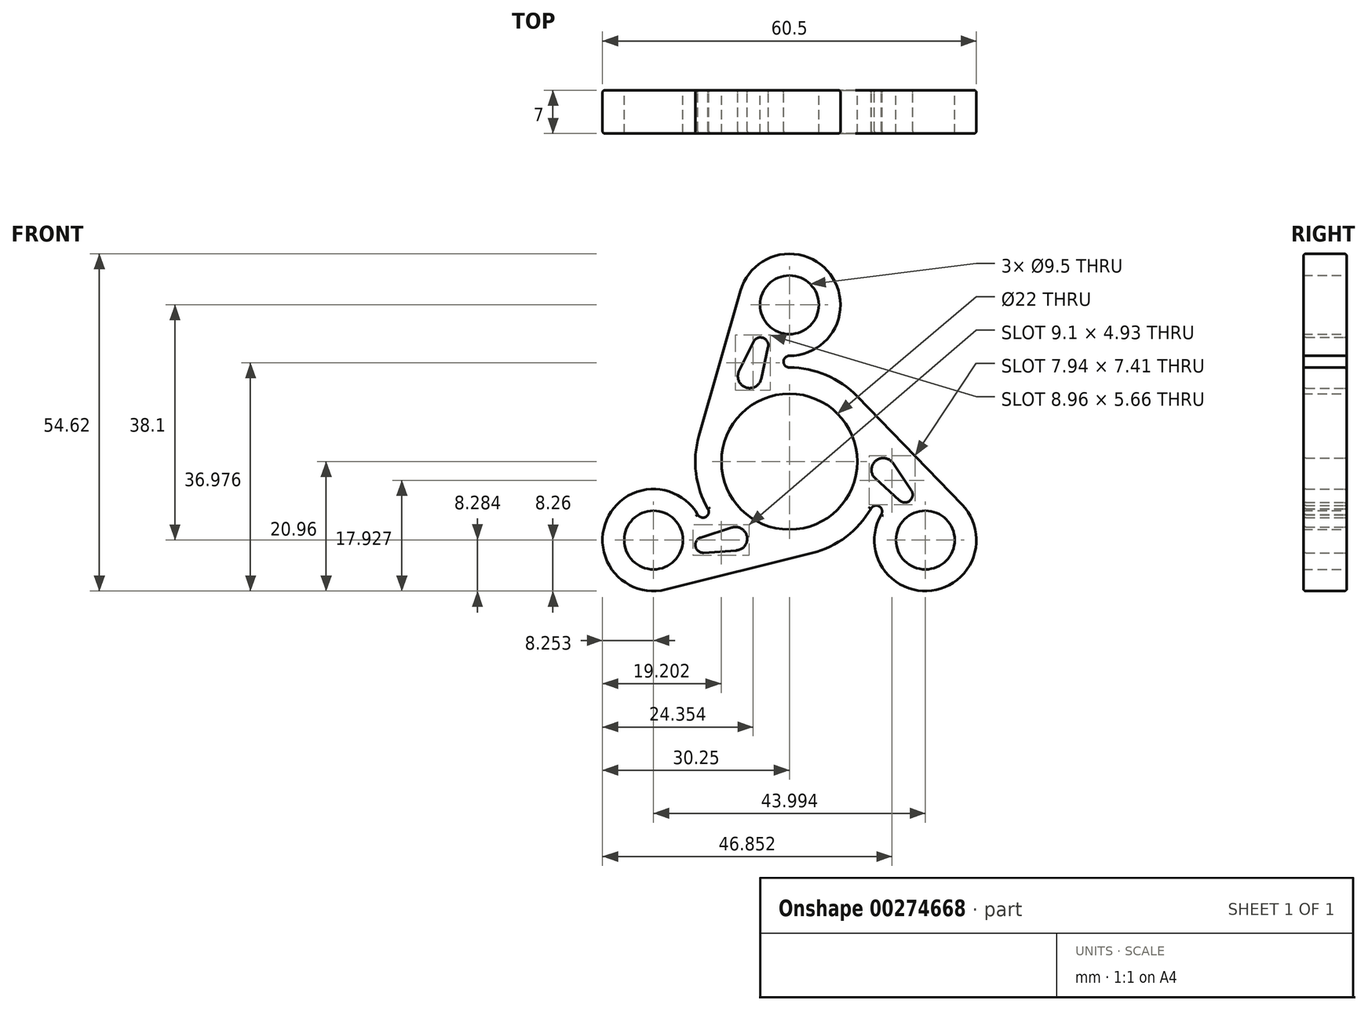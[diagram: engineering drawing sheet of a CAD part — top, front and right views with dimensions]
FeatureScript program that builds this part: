
annotation { "Feature Type Name" : "Feature", "Feature Type Description" : "" }
export const myFeature = defineFeature(function(context is Context, id is Id, definition is map)
    precondition{}
    {
        {
            var Q0;
            Q0=qCreatedBy(makeId("Front.planeOp"),FACE);
            var sketch = newSketch(context, id + "F0", { "sketchPlane" : qUnion([Q0])});
            skCircle(sketch, "E0", {"center": v(0, 0) * mm, "radius": 11 * mm});
            skArc(sketch, "E1", {"start": v(-14.65, 4.2) * mm, "mid": v(-15.12, -1.88) * mm, "end": v(-13.18, -7.66) * mm});
            skLineSegment(sketch, "E2", {"start": v(0, 0) * mm, "end": v(-45.3, -26.16) * mm, "construction": true});
            skLineSegment(sketch, "E3", {"start": v(0, 0) * mm, "end": v(47.1, -27.19) * mm, "construction": true});
            skCircle(sketch, "E4", {"center": v(0, 0) * mm, "radius": 25.4 * mm, "construction": true});
            skCircle(sketch, "E5", {"center": v(0, 25.4) * mm, "radius": 4.75 * mm});
            skCircle(sketch, "E6", {"center": v(-22, -12.7) * mm, "radius": 4.75 * mm});
            skCircle(sketch, "E7", {"center": v(22, -12.7) * mm, "radius": 4.75 * mm});
            skArc(sketch, "E8", {"start": v(0, 17.14) * mm, "mid": v(6.6, 30.37) * mm, "end": v(-7.94, 27.67) * mm});
            skArc(sketch, "E9", {"start": v(-14.83, -8.6) * mm, "mid": v(-29.59, -9.46) * mm, "end": v(-20, -20.7) * mm});
            skArc(sketch, "E10", {"start": v(14.85, -8.57) * mm, "mid": v(23, -20.9) * mm, "end": v(27.93, -6.96) * mm});
            skLineSegment(sketch, "E11", {"start": v(-7.94, 27.67) * mm, "end": v(-14.65, 4.2) * mm});
            skLineSegment(sketch, "E12", {"start": v(-20, -20.7) * mm, "end": v(3.7, -14.78) * mm});
            skLineSegment(sketch, "E13", {"start": v(27.93, -6.96) * mm, "end": v(10.96, 10.6) * mm});
            skArc(sketch, "E14.trimOffspring", {"start": v(10.96, 10.6) * mm, "mid": v(5.95, 14.03) * mm, "end": v(0, 15.24) * mm});
            skArc(sketch, "E15.trimOffspring", {"start": v(3.7, -14.78) * mm, "mid": v(9.18, -12.17) * mm, "end": v(13.2, -7.62) * mm});
            skArc(sketch, "E16", {"start": v(-8.15, 14.65) * mm, "mid": v(-7.06, 12.01) * mm, "end": v(-4.58, 13.4) * mm});
            skLineSegment(sketch, "E17", {"start": v(-6.44, 13.81) * mm, "end": v(0, 0) * mm, "construction": true});
            skArc(sketch, "E18", {"start": v(-3.46, 18.58) * mm, "mid": v(-4.28, 20.05) * mm, "end": v(-5.84, 19.4) * mm});
            skLineSegment(sketch, "E19", {"start": v(-3.46, 18.58) * mm, "end": v(-4.58, 13.4) * mm});
            skLineSegment(sketch, "E20", {"start": v(-5.84, 19.4) * mm, "end": v(-8.15, 14.65) * mm});
            skLineSegment(sketch, "E21.1.0", {"start": v(-13.88, -14.76) * mm, "end": v(-8.6, -14.38) * mm});
            skArc(sketch, "E21.1.1", {"start": v(-14.36, -12.28) * mm, "mid": v(-15.22, -13.73) * mm, "end": v(-13.88, -14.76) * mm});
            skLineSegment(sketch, "E21.1.2", {"start": v(-14.36, -12.28) * mm, "end": v(-9.32, -10.67) * mm});
            skArc(sketch, "E21.1.3", {"start": v(-8.6, -14.38) * mm, "mid": v(-6.87, -12.12) * mm, "end": v(-9.32, -10.67) * mm});
            skLineSegment(sketch, "E21.2.0", {"start": v(19.72, -4.64) * mm, "end": v(16.76, -0.26) * mm});
            skArc(sketch, "E21.2.1", {"start": v(17.82, -6.3) * mm, "mid": v(19.5, -6.31) * mm, "end": v(19.72, -4.64) * mm});
            skLineSegment(sketch, "E21.2.2", {"start": v(17.82, -6.3) * mm, "end": v(13.9, -2.74) * mm});
            skArc(sketch, "E21.2.3", {"start": v(16.76, -0.26) * mm, "mid": v(13.93, 0.11) * mm, "end": v(13.9, -2.74) * mm});
            skLineSegment(sketch, "E22", {"start": v(0, 0) * mm, "end": v(-4.7, 18.85) * mm, "construction": true});
            skArc(sketch, "E23", {"start": v(-14.85, -8.57) * mm, "mid": v(-13.54, -8.94) * mm, "end": v(-13.2, -7.62) * mm});
            skArc(sketch, "E24", {"start": v(0, 17.14) * mm, "mid": v(-0.95, 16.2) * mm, "end": v(0, 15.24) * mm});
            skArc(sketch, "E25", {"start": v(14.85, -8.57) * mm, "mid": v(14.52, -7.23) * mm, "end": v(13.2, -7.62) * mm});
            skSolve(sketch);
        }
        {
            var Q0;
            Q0 = qSketchRegion(id + "F0", true);
            extrude(context, id + "F1", {"entities" : qUnion([Q0]), "depth" : 7 * mm, "offsetDistance" : 25.4 * mm});
        }
        {
            var Q0;
            Q0=makeQuery(id+"F1.opExtrude","CAP_EDGE",EDGE,{"disambiguationData":[OSD([sQuery(id+"F0.wireOp",EDGE,"E1")])],"isStart":false});
            var Q1;
            Q1=makeQuery(id+"F1.opExtrude","CAP_EDGE",EDGE,{"disambiguationData":[OSD([sQuery(id+"F0.wireOp",EDGE,"E11")])],"isStart":false});
            var Q2;
            Q2=makeQuery(id+"F1.opExtrude","CAP_EDGE",EDGE,{"disambiguationData":[OSD([sQuery(id+"F0.wireOp",EDGE,"E16")])],"isStart":false});
            var Q3;
            Q3=makeQuery(id+"F1.opExtrude","CAP_EDGE",EDGE,{"disambiguationData":[OSD([sQuery(id+"F0.wireOp",EDGE,"E19")])],"isStart":false});
            var Q4;
            Q4=makeQuery(id+"F1.opExtrude","CAP_EDGE",EDGE,{"disambiguationData":[OSD([sQuery(id+"F0.wireOp",EDGE,"E20")])],"isStart":false});
            var Q5;
            Q5=makeQuery(id+"F1.opExtrude","CAP_EDGE",EDGE,{"disambiguationData":[OSD([sQuery(id+"F0.wireOp",EDGE,"E18")])],"isStart":false});
            var Q6;
            Q6=makeQuery(id+"F1.opExtrude","CAP_EDGE",EDGE,{"disambiguationData":[OSD([sQuery(id+"F0.wireOp",EDGE,"E8")])],"isStart":false});
            var Q7;
            Q7=makeQuery(id+"F1.opExtrude","CAP_EDGE",EDGE,{"disambiguationData":[OSD([sQuery(id+"F0.wireOp",EDGE,"E24")])],"isStart":false});
            var Q8;
            Q8=makeQuery(id+"F1.opExtrude","CAP_EDGE",EDGE,{"disambiguationData":[OSD([sQuery(id+"F0.wireOp",EDGE,"E14.trimOffspring")])],"isStart":false});
            var Q9;
            Q9=makeQuery(id+"F1.opExtrude","CAP_EDGE",EDGE,{"disambiguationData":[OSD([sQuery(id+"F0.wireOp",EDGE,"E13")])],"isStart":false});
            var Q10;
            Q10=makeQuery(id+"F1.opExtrude","CAP_EDGE",EDGE,{"disambiguationData":[OSD([sQuery(id+"F0.wireOp",EDGE,"E25")])],"isStart":false});
            var Q11;
            Q11=makeQuery(id+"F1.opExtrude","CAP_EDGE",EDGE,{"disambiguationData":[OSD([sQuery(id+"F0.wireOp",EDGE,"E15.trimOffspring")])],"isStart":false});
            var Q12;
            Q12=makeQuery(id+"F1.opExtrude","CAP_EDGE",EDGE,{"disambiguationData":[OSD([sQuery(id+"F0.wireOp",EDGE,"E21.2.3")])],"isStart":false});
            var Q13;
            Q13=makeQuery(id+"F1.opExtrude","CAP_EDGE",EDGE,{"disambiguationData":[OSD([sQuery(id+"F0.wireOp",EDGE,"E21.2.2")])],"isStart":false});
            var Q14;
            Q14=makeQuery(id+"F1.opExtrude","CAP_EDGE",EDGE,{"disambiguationData":[OSD([sQuery(id+"F0.wireOp",EDGE,"E21.2.0")])],"isStart":false});
            var Q15;
            Q15=makeQuery(id+"F1.opExtrude","CAP_EDGE",EDGE,{"disambiguationData":[OSD([sQuery(id+"F0.wireOp",EDGE,"E21.2.1")])],"isStart":false});
            var Q16;
            Q16=makeQuery(id+"F1.opExtrude","CAP_EDGE",EDGE,{"disambiguationData":[OSD([sQuery(id+"F0.wireOp",EDGE,"E21.1.3")])],"isStart":false});
            var Q17;
            Q17=makeQuery(id+"F1.opExtrude","CAP_EDGE",EDGE,{"disambiguationData":[OSD([sQuery(id+"F0.wireOp",EDGE,"E21.1.2")])],"isStart":false});
            var Q18;
            Q18=makeQuery(id+"F1.opExtrude","CAP_EDGE",EDGE,{"disambiguationData":[OSD([sQuery(id+"F0.wireOp",EDGE,"E21.1.0")])],"isStart":false});
            var Q19;
            Q19=makeQuery(id+"F1.opExtrude","CAP_EDGE",EDGE,{"disambiguationData":[OSD([sQuery(id+"F0.wireOp",EDGE,"E21.1.1")])],"isStart":false});
            var Q20;
            Q20=makeQuery(id+"F1.opExtrude","CAP_EDGE",EDGE,{"disambiguationData":[OSD([sQuery(id+"F0.wireOp",EDGE,"E23")])],"isStart":false});
            var Q21;
            Q21=makeQuery(id+"F1.opExtrude","CAP_EDGE",EDGE,{"disambiguationData":[OSD([sQuery(id+"F0.wireOp",EDGE,"E12")])],"isStart":false});
            var Q22;
            Q22=makeQuery(id+"F1.opExtrude","CAP_EDGE",EDGE,{"disambiguationData":[OSD([sQuery(id+"F0.wireOp",EDGE,"E8")])],"isStart":true});
            var Q23;
            Q23=makeQuery(id+"F1.opExtrude","CAP_EDGE",EDGE,{"disambiguationData":[OSD([sQuery(id+"F0.wireOp",EDGE,"E11")])],"isStart":true});
            var Q24;
            Q24=makeQuery(id+"F1.opExtrude","CAP_EDGE",EDGE,{"disambiguationData":[OSD([sQuery(id+"F0.wireOp",EDGE,"E1")])],"isStart":true});
            var Q25;
            Q25=makeQuery(id+"F1.opExtrude","CAP_EDGE",EDGE,{"disambiguationData":[OSD([sQuery(id+"F0.wireOp",EDGE,"E23")])],"isStart":true});
            var Q26;
            Q26=makeQuery(id+"F1.opExtrude","CAP_EDGE",EDGE,{"disambiguationData":[OSD([sQuery(id+"F0.wireOp",EDGE,"E9")])],"isStart":true});
            var Q27;
            Q27=makeQuery(id+"F1.opExtrude","CAP_EDGE",EDGE,{"disambiguationData":[OSD([sQuery(id+"F0.wireOp",EDGE,"E12")])],"isStart":true});
            var Q28;
            Q28=makeQuery(id+"F1.opExtrude","CAP_EDGE",EDGE,{"disambiguationData":[OSD([sQuery(id+"F0.wireOp",EDGE,"E15.trimOffspring")])],"isStart":true});
            var Q29;
            Q29=makeQuery(id+"F1.opExtrude","CAP_EDGE",EDGE,{"disambiguationData":[OSD([sQuery(id+"F0.wireOp",EDGE,"E25")])],"isStart":true});
            var Q30;
            Q30=makeQuery(id+"F1.opExtrude","CAP_EDGE",EDGE,{"disambiguationData":[OSD([sQuery(id+"F0.wireOp",EDGE,"E21.2.0")])],"isStart":true});
            var Q31;
            Q31=makeQuery(id+"F1.opExtrude","CAP_EDGE",EDGE,{"disambiguationData":[OSD([sQuery(id+"F0.wireOp",EDGE,"E21.2.3")])],"isStart":true});
            var Q32;
            Q32=makeQuery(id+"F1.opExtrude","CAP_EDGE",EDGE,{"disambiguationData":[OSD([sQuery(id+"F0.wireOp",EDGE,"E21.2.1")])],"isStart":true});
            var Q33;
            Q33=makeQuery(id+"F1.opExtrude","CAP_EDGE",EDGE,{"disambiguationData":[OSD([sQuery(id+"F0.wireOp",EDGE,"E21.1.2")])],"isStart":true});
            var Q34;
            Q34=makeQuery(id+"F1.opExtrude","CAP_EDGE",EDGE,{"disambiguationData":[OSD([sQuery(id+"F0.wireOp",EDGE,"E20")])],"isStart":true});
            fillet(context, id + "F2", {"entities" : qUnion([Q0, Q1, Q2, Q3, Q4, Q5, Q6, Q7, Q8, Q9, Q10, Q11, Q12, Q13, Q14, Q15, Q16, Q17, Q18, Q19, Q20, Q21, Q22, Q23, Q24, Q25, Q26, Q27, Q28, Q29, Q30, Q31, Q32, Q33, Q34]), "radius" : 0.38 * mm, "tangentPropagation" : true, "allowEdgeOverflow" : false});
        }
    });
